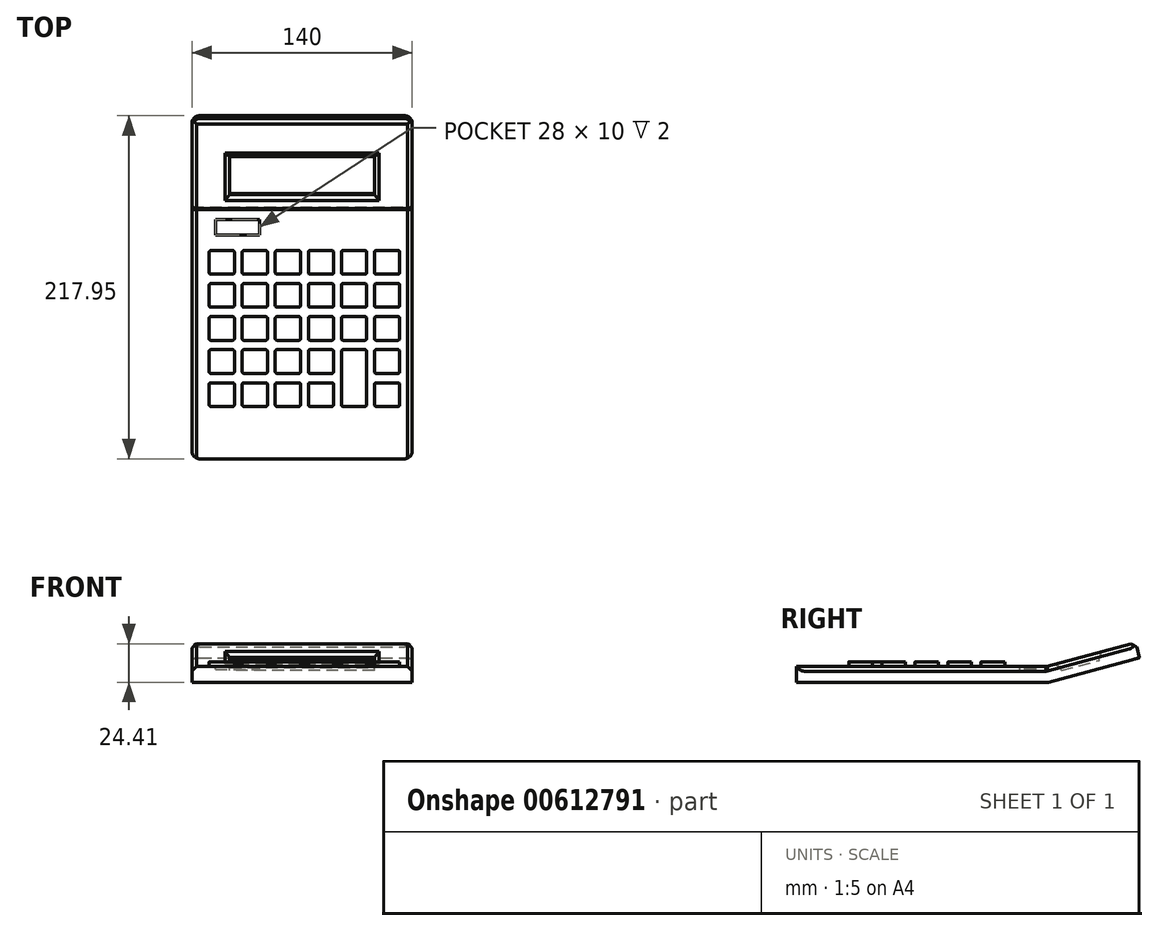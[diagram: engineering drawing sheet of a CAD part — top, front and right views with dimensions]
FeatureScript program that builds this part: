
annotation { "Feature Type Name" : "Feature", "Feature Type Description" : "" }
export const myFeature = defineFeature(function(context is Context, id is Id, definition is map)
    precondition{}
    {
        {
            var Q0;
            Q0=qCreatedBy(makeId("Right.planeOp"),FACE);
            var sketch = newSketch(context, id + "F0", { "sketchPlane" : qUnion([Q0])});
            skLineSegment(sketch, "E0", {"start": v(-151.78, 0) * mm, "end": v(8.22, 0) * mm});
            skLineSegment(sketch, "E1", {"start": v(8.22, 0) * mm, "end": v(66.17, 15.53) * mm});
            skLineSegment(sketch, "E2.0", {"start": v(6.9, 10) * mm, "end": v(63.58, 25.19) * mm});
            skLineSegment(sketch, "E2.1", {"start": v(-151.78, 10) * mm, "end": v(6.9, 10) * mm});
            skLineSegment(sketch, "E3", {"start": v(-151.78, 0) * mm, "end": v(-151.78, 10) * mm});
            skLineSegment(sketch, "E4", {"start": v(66.17, 15.53) * mm, "end": v(63.58, 25.19) * mm});
            skSolve(sketch);
        }
        {
            var Q0;
            Q0 = qSketchRegion(id + "F0", true);
            extrude(context, id + "F1", {"entities" : qUnion([Q0]), "endBound" : BoundingType.SYMMETRIC, "oppositeDirection" : true, "depth" : 140 * mm, "offsetDistance" : 25 * mm});
        }
        {
            var Q0;
            Q0=makeQuery(id+"F1.opExtrude","SWEPT_FACE",FACE,{"disambiguationData":[OSD([sQuery(id+"F0.wireOp",EDGE,"E2.0")])]});
            var sketch = newSketch(context, id + "F2", { "sketchPlane" : qUnion([Q0])});
            skLineSegment(sketch, "E5.bottom", {"start": v(46, 17.94) * mm, "end": v(-46, 17.94) * mm});
            skLineSegment(sketch, "E5.top", {"start": v(46, 42.94) * mm, "end": v(-46, 42.94) * mm});
            skLineSegment(sketch, "E5.left", {"start": v(46, 17.94) * mm, "end": v(46, 42.94) * mm});
            skLineSegment(sketch, "E5.right", {"start": v(-46, 17.94) * mm, "end": v(-46, 42.94) * mm});
            skPoint(sketch, "E5.middle", {"position": v(0, 30.44) * mm});
            skPoint(sketch, "E5.middle.positionSnap0", {"position": v(0, 9.25) * mm});
            skPoint(sketch, "E5.centerSnap0", {"position": v(0, 9.25) * mm});
            skSolve(sketch);
        }
        {
            var Q0;
            Q0 = qSketchRegion(id + "F2", true);
            extrude(context, id + "F3", {"entities" : qUnion([Q0]), "operationType" : NewBodyOperationType.REMOVE, "oppositeDirection" : true, "depth" : 5 * mm, "offsetDistance" : 25 * mm});
        }
        {
            var Q0;
            Q0=makeQuery(id+"F3.boolean.opBoolean","COPY",EDGE,{"derivedFrom":makeQuery(id+"F3.opExtrude","CAP_EDGE",EDGE,{"disambiguationData":[OSD([sQuery(id+"F2.wireOp",EDGE,"E5.right")])],"isStart":true})});
            var Q1;
            Q1=makeQuery(id+"F3.boolean.opBoolean","COPY",EDGE,{"derivedFrom":makeQuery(id+"F3.opExtrude","CAP_EDGE",EDGE,{"disambiguationData":[OSD([sQuery(id+"F2.wireOp",EDGE,"E5.top")])],"isStart":true})});
            var Q2;
            Q2=makeQuery(id+"F1.opExtrude","SWEPT_FACE",FACE,{"disambiguationData":[OSD([sQuery(id+"F0.wireOp",EDGE,"E2.0")])]});
            chamfer(context, id + "F4", {"entities" : qUnion([Q0, Q1, Q2]), "width" : 3 * mm, "tangentPropagation" : true});
        }
        {
            var Q0;
            Q0=makeQuery(id+"F1.opExtrude","CAP_EDGE",EDGE,{"disambiguationData":[OSD([sQuery(id+"F0.wireOp",EDGE,"E3")])],"isStart":false});
            var Q1;
            Q1=makeQuery(id+"F1.opExtrude","CAP_EDGE",EDGE,{"disambiguationData":[OSD([sQuery(id+"F0.wireOp",EDGE,"E3")])],"isStart":true});
            var Q2;
            Q2=makeQuery(id+"F1.opExtrude","CAP_EDGE",EDGE,{"disambiguationData":[OSD([sQuery(id+"F0.wireOp",EDGE,"E4")])],"isStart":false});
            var Q3;
            Q3=makeQuery(id+"F1.opExtrude","CAP_EDGE",EDGE,{"disambiguationData":[OSD([sQuery(id+"F0.wireOp",EDGE,"E4")])],"isStart":true});
            fillet(context, id + "F5", {"entities" : qUnion([Q0, Q1, Q2, Q3]), "radius" : 5 * mm, "tangentPropagation" : true, "allowEdgeOverflow" : false});
        }
        {
            var Q0;
            Q0=makeQuery(id+"F1.opExtrude","SWEPT_FACE",FACE,{"disambiguationData":[OSD([sQuery(id+"F0.wireOp",EDGE,"E2.1")])]});
            var sketch = newSketch(context, id + "F6", { "sketchPlane" : qUnion([Q0])});
            skLineSegment(sketch, "E6.bottom", {"start": v(-58, -19.5) * mm, "end": v(-44, -19.5) * mm});
            skLineSegment(sketch, "E6.top", {"start": v(-58, -34.5) * mm, "end": v(-44, -34.5) * mm});
            skLineSegment(sketch, "E6.left", {"start": v(-59, -20.5) * mm, "end": v(-59, -33.5) * mm});
            skLineSegment(sketch, "E6.right", {"start": v(-43, -20.5) * mm, "end": v(-43, -33.5) * mm});
            skLineSegment(sketch, "E7.bottom", {"start": v(-55, 0.28) * mm, "end": v(-27, 0.28) * mm});
            skLineSegment(sketch, "E7.top", {"start": v(-55, -9.72) * mm, "end": v(-27, -9.72) * mm});
            skLineSegment(sketch, "E7.left", {"start": v(-55, 0.28) * mm, "end": v(-55, -9.72) * mm});
            skLineSegment(sketch, "E7.right", {"start": v(-27, 0.28) * mm, "end": v(-27, -9.72) * mm});
            skPoint(sketch, "E8.visualSharp", {"position": v(-43, -19.5) * mm});
            skArc(sketch, "E8.filletArc", {"start": v(-43, -20.5) * mm, "mid": v(-43.3, -19.79) * mm, "end": v(-44, -19.5) * mm});
            skPoint(sketch, "E9.visualSharp", {"position": v(-43, -34.5) * mm});
            skArc(sketch, "E9.filletArc", {"start": v(-44, -34.5) * mm, "mid": v(-43.3, -34.2) * mm, "end": v(-43, -33.5) * mm});
            skPoint(sketch, "E10.visualSharp", {"position": v(-59, -34.5) * mm});
            skArc(sketch, "E10.filletArc", {"start": v(-59, -33.5) * mm, "mid": v(-58.7, -34.2) * mm, "end": v(-58, -34.5) * mm});
            skPoint(sketch, "E11.visualSharp", {"position": v(-59, -19.5) * mm});
            skArc(sketch, "E11.filletArc", {"start": v(-58, -19.5) * mm, "mid": v(-58.7, -19.79) * mm, "end": v(-59, -20.5) * mm});
            skPoint(sketch, "E12.1.0.0", {"position": v(-22, -19.5) * mm});
            skLineSegment(sketch, "E12.1.0.1", {"start": v(-38, -20.5) * mm, "end": v(-38, -33.5) * mm});
            skPoint(sketch, "E12.1.0.2", {"position": v(-22, -34.5) * mm});
            skLineSegment(sketch, "E12.1.0.3", {"start": v(-37, -34.5) * mm, "end": v(-23, -34.5) * mm});
            skLineSegment(sketch, "E12.1.0.4", {"start": v(-22, -20.5) * mm, "end": v(-22, -33.5) * mm});
            skLineSegment(sketch, "E12.1.0.5", {"start": v(-37, -19.5) * mm, "end": v(-23, -19.5) * mm});
            skPoint(sketch, "E12.1.0.6", {"position": v(-38, -19.5) * mm});
            skPoint(sketch, "E12.1.0.7", {"position": v(-38, -34.5) * mm});
            skArc(sketch, "E12.1.0.8", {"start": v(-23, -34.5) * mm, "mid": v(-22.3, -34.2) * mm, "end": v(-22, -33.5) * mm});
            skArc(sketch, "E12.1.0.9", {"start": v(-37, -19.5) * mm, "mid": v(-37.7, -19.79) * mm, "end": v(-38, -20.5) * mm});
            skArc(sketch, "E12.1.0.10", {"start": v(-38, -33.5) * mm, "mid": v(-37.7, -34.2) * mm, "end": v(-37, -34.5) * mm});
            skArc(sketch, "E12.1.0.11", {"start": v(-22, -20.5) * mm, "mid": v(-22.3, -19.79) * mm, "end": v(-23, -19.5) * mm});
            skPoint(sketch, "E12.2.0.0", {"position": v(-1, -19.5) * mm});
            skLineSegment(sketch, "E12.2.0.1", {"start": v(-17, -20.5) * mm, "end": v(-17, -33.5) * mm});
            skPoint(sketch, "E12.2.0.2", {"position": v(-1, -34.5) * mm});
            skLineSegment(sketch, "E12.2.0.3", {"start": v(-16, -34.5) * mm, "end": v(-2, -34.5) * mm});
            skLineSegment(sketch, "E12.2.0.4", {"start": v(-1, -20.5) * mm, "end": v(-1, -33.5) * mm});
            skLineSegment(sketch, "E12.2.0.5", {"start": v(-16, -19.5) * mm, "end": v(-2, -19.5) * mm});
            skPoint(sketch, "E12.2.0.6", {"position": v(-17, -19.5) * mm});
            skPoint(sketch, "E12.2.0.7", {"position": v(-17, -34.5) * mm});
            skArc(sketch, "E12.2.0.8", {"start": v(-2, -34.5) * mm, "mid": v(-1.3, -34.2) * mm, "end": v(-1, -33.5) * mm});
            skArc(sketch, "E12.2.0.9", {"start": v(-16, -19.5) * mm, "mid": v(-16.7, -19.79) * mm, "end": v(-17, -20.5) * mm});
            skArc(sketch, "E12.2.0.10", {"start": v(-17, -33.5) * mm, "mid": v(-16.7, -34.2) * mm, "end": v(-16, -34.5) * mm});
            skArc(sketch, "E12.2.0.11", {"start": v(-1, -20.5) * mm, "mid": v(-1.3, -19.79) * mm, "end": v(-2, -19.5) * mm});
            skPoint(sketch, "E12.3.0.0", {"position": v(20, -19.5) * mm});
            skLineSegment(sketch, "E12.3.0.1", {"start": v(4, -20.5) * mm, "end": v(4, -33.5) * mm});
            skPoint(sketch, "E12.3.0.2", {"position": v(20, -34.5) * mm});
            skLineSegment(sketch, "E12.3.0.3", {"start": v(5, -34.5) * mm, "end": v(19, -34.5) * mm});
            skLineSegment(sketch, "E12.3.0.4", {"start": v(20, -20.5) * mm, "end": v(20, -33.5) * mm});
            skLineSegment(sketch, "E12.3.0.5", {"start": v(5, -19.5) * mm, "end": v(19, -19.5) * mm});
            skPoint(sketch, "E12.3.0.6", {"position": v(4, -19.5) * mm});
            skPoint(sketch, "E12.3.0.7", {"position": v(4, -34.5) * mm});
            skArc(sketch, "E12.3.0.8", {"start": v(19, -34.5) * mm, "mid": v(19.7, -34.2) * mm, "end": v(20, -33.5) * mm});
            skArc(sketch, "E12.3.0.9", {"start": v(5, -19.5) * mm, "mid": v(4.3, -19.79) * mm, "end": v(4, -20.5) * mm});
            skArc(sketch, "E12.3.0.10", {"start": v(4, -33.5) * mm, "mid": v(4.3, -34.2) * mm, "end": v(5, -34.5) * mm});
            skArc(sketch, "E12.3.0.11", {"start": v(20, -20.5) * mm, "mid": v(19.7, -19.79) * mm, "end": v(19, -19.5) * mm});
            skPoint(sketch, "E12.4.0.0", {"position": v(41, -19.5) * mm});
            skLineSegment(sketch, "E12.4.0.1", {"start": v(25, -20.5) * mm, "end": v(25, -33.5) * mm});
            skPoint(sketch, "E12.4.0.2", {"position": v(41, -34.5) * mm});
            skLineSegment(sketch, "E12.4.0.3", {"start": v(26, -34.5) * mm, "end": v(40, -34.5) * mm});
            skLineSegment(sketch, "E12.4.0.4", {"start": v(41, -20.5) * mm, "end": v(41, -33.5) * mm});
            skLineSegment(sketch, "E12.4.0.5", {"start": v(26, -19.5) * mm, "end": v(40, -19.5) * mm});
            skPoint(sketch, "E12.4.0.6", {"position": v(25, -19.5) * mm});
            skPoint(sketch, "E12.4.0.7", {"position": v(25, -34.5) * mm});
            skArc(sketch, "E12.4.0.8", {"start": v(40, -34.5) * mm, "mid": v(40.7, -34.2) * mm, "end": v(41, -33.5) * mm});
            skArc(sketch, "E12.4.0.9", {"start": v(26, -19.5) * mm, "mid": v(25.3, -19.79) * mm, "end": v(25, -20.5) * mm});
            skArc(sketch, "E12.4.0.10", {"start": v(25, -33.5) * mm, "mid": v(25.3, -34.2) * mm, "end": v(26, -34.5) * mm});
            skArc(sketch, "E12.4.0.11", {"start": v(41, -20.5) * mm, "mid": v(40.7, -19.79) * mm, "end": v(40, -19.5) * mm});
            skPoint(sketch, "E12.5.0.0", {"position": v(62, -19.5) * mm});
            skLineSegment(sketch, "E12.5.0.1", {"start": v(46, -20.5) * mm, "end": v(46, -33.5) * mm});
            skPoint(sketch, "E12.5.0.2", {"position": v(62, -34.5) * mm});
            skLineSegment(sketch, "E12.5.0.3", {"start": v(47, -34.5) * mm, "end": v(61, -34.5) * mm});
            skLineSegment(sketch, "E12.5.0.4", {"start": v(62, -20.5) * mm, "end": v(62, -33.5) * mm});
            skLineSegment(sketch, "E12.5.0.5", {"start": v(47, -19.5) * mm, "end": v(61, -19.5) * mm});
            skPoint(sketch, "E12.5.0.6", {"position": v(46, -19.5) * mm});
            skPoint(sketch, "E12.5.0.7", {"position": v(46, -34.5) * mm});
            skArc(sketch, "E12.5.0.8", {"start": v(61, -34.5) * mm, "mid": v(61.7, -34.2) * mm, "end": v(62, -33.5) * mm});
            skArc(sketch, "E12.5.0.9", {"start": v(47, -19.5) * mm, "mid": v(46.3, -19.79) * mm, "end": v(46, -20.5) * mm});
            skArc(sketch, "E12.5.0.10", {"start": v(46, -33.5) * mm, "mid": v(46.3, -34.2) * mm, "end": v(47, -34.5) * mm});
            skArc(sketch, "E12.5.0.11", {"start": v(62, -20.5) * mm, "mid": v(61.7, -19.79) * mm, "end": v(61, -19.5) * mm});
            skLineSegment(sketch, "E12.direction1", {"start": v(-59, -34.5) * mm, "end": v(-38, -34.5) * mm, "construction": true});
            skPoint(sketch, "E13.0.1.0", {"position": v(-59, -40.5) * mm});
            skLineSegment(sketch, "E13.0.1.1", {"start": v(26, -40.5) * mm, "end": v(40, -40.5) * mm});
            skLineSegment(sketch, "E13.0.1.2", {"start": v(-16, -40.5) * mm, "end": v(-2, -40.5) * mm});
            skPoint(sketch, "E13.0.1.3", {"position": v(4, -40.5) * mm});
            skLineSegment(sketch, "E13.0.1.4", {"start": v(5, -55.5) * mm, "end": v(19, -55.5) * mm});
            skPoint(sketch, "E13.0.1.5", {"position": v(62, -40.5) * mm});
            skPoint(sketch, "E13.0.1.6", {"position": v(-1, -40.5) * mm});
            skLineSegment(sketch, "E13.0.1.7", {"start": v(-59, -55.5) * mm, "end": v(-38, -55.5) * mm, "construction": true});
            skPoint(sketch, "E13.0.1.8", {"position": v(-22, -40.5) * mm});
            skPoint(sketch, "E13.0.1.9", {"position": v(-22, -55.5) * mm});
            skPoint(sketch, "E13.0.1.10", {"position": v(25, -55.5) * mm});
            skPoint(sketch, "E13.0.1.11", {"position": v(20, -55.5) * mm});
            skPoint(sketch, "E13.0.1.12", {"position": v(-17, -55.5) * mm});
            skPoint(sketch, "E13.0.1.13", {"position": v(20, -40.5) * mm});
            skLineSegment(sketch, "E13.0.1.14", {"start": v(25, -41.5) * mm, "end": v(25, -54.5) * mm});
            skPoint(sketch, "E13.0.1.15", {"position": v(62, -55.5) * mm});
            skPoint(sketch, "E13.0.1.16", {"position": v(41, -40.5) * mm});
            skLineSegment(sketch, "E13.0.1.17", {"start": v(-17, -41.5) * mm, "end": v(-17, -54.5) * mm});
            skLineSegment(sketch, "E13.0.1.18", {"start": v(47, -55.5) * mm, "end": v(61, -55.5) * mm});
            skPoint(sketch, "E13.0.1.19", {"position": v(46, -40.5) * mm});
            skPoint(sketch, "E13.0.1.20", {"position": v(-38, -40.5) * mm});
            skPoint(sketch, "E13.0.1.21", {"position": v(41, -55.5) * mm});
            skPoint(sketch, "E13.0.1.22", {"position": v(-1, -55.5) * mm});
            skPoint(sketch, "E13.0.1.23", {"position": v(-38, -55.5) * mm});
            skPoint(sketch, "E13.0.1.24", {"position": v(-59, -55.5) * mm});
            skPoint(sketch, "E13.0.1.25", {"position": v(46, -55.5) * mm});
            skPoint(sketch, "E13.0.1.26", {"position": v(4, -55.5) * mm});
            skLineSegment(sketch, "E13.0.1.27", {"start": v(46, -41.5) * mm, "end": v(46, -54.5) * mm});
            skLineSegment(sketch, "E13.0.1.28", {"start": v(4, -41.5) * mm, "end": v(4, -54.5) * mm});
            skLineSegment(sketch, "E13.0.1.29", {"start": v(62, -41.5) * mm, "end": v(62, -54.5) * mm});
            skLineSegment(sketch, "E13.0.1.30", {"start": v(26, -55.5) * mm, "end": v(40, -55.5) * mm});
            skLineSegment(sketch, "E13.0.1.31", {"start": v(20, -41.5) * mm, "end": v(20, -54.5) * mm});
            skLineSegment(sketch, "E13.0.1.32", {"start": v(-16, -55.5) * mm, "end": v(-2, -55.5) * mm});
            skPoint(sketch, "E13.0.1.33", {"position": v(25, -40.5) * mm});
            skPoint(sketch, "E13.0.1.34", {"position": v(-17, -40.5) * mm});
            skPoint(sketch, "E13.0.1.35", {"position": v(-43, -55.5) * mm});
            skLineSegment(sketch, "E13.0.1.36", {"start": v(-37, -55.5) * mm, "end": v(-23, -55.5) * mm});
            skLineSegment(sketch, "E13.0.1.37", {"start": v(-22, -41.5) * mm, "end": v(-22, -54.5) * mm});
            skLineSegment(sketch, "E13.0.1.38", {"start": v(-37, -40.5) * mm, "end": v(-23, -40.5) * mm});
            skLineSegment(sketch, "E13.0.1.39", {"start": v(-59, -41.5) * mm, "end": v(-59, -54.5) * mm});
            skLineSegment(sketch, "E13.0.1.40", {"start": v(-43, -41.5) * mm, "end": v(-43, -54.5) * mm});
            skLineSegment(sketch, "E13.0.1.41", {"start": v(47, -40.5) * mm, "end": v(61, -40.5) * mm});
            skLineSegment(sketch, "E13.0.1.42", {"start": v(41, -41.5) * mm, "end": v(41, -54.5) * mm});
            skLineSegment(sketch, "E13.0.1.43", {"start": v(5, -40.5) * mm, "end": v(19, -40.5) * mm});
            skLineSegment(sketch, "E13.0.1.44", {"start": v(-1, -41.5) * mm, "end": v(-1, -54.5) * mm});
            skLineSegment(sketch, "E13.0.1.45", {"start": v(-38, -41.5) * mm, "end": v(-38, -54.5) * mm});
            skPoint(sketch, "E13.0.1.46", {"position": v(-43, -40.5) * mm});
            skLineSegment(sketch, "E13.0.1.47", {"start": v(-58, -40.5) * mm, "end": v(-44, -40.5) * mm});
            skLineSegment(sketch, "E13.0.1.48", {"start": v(-58, -55.5) * mm, "end": v(-44, -55.5) * mm});
            skArc(sketch, "E13.0.1.49", {"start": v(19, -55.5) * mm, "mid": v(19.7, -55.2) * mm, "end": v(20, -54.5) * mm});
            skArc(sketch, "E13.0.1.50", {"start": v(62, -41.5) * mm, "mid": v(61.7, -40.79) * mm, "end": v(61, -40.5) * mm});
            skArc(sketch, "E13.0.1.51", {"start": v(47, -40.5) * mm, "mid": v(46.3, -40.79) * mm, "end": v(46, -41.5) * mm});
            skArc(sketch, "E13.0.1.52", {"start": v(25, -54.5) * mm, "mid": v(25.3, -55.2) * mm, "end": v(26, -55.5) * mm});
            skArc(sketch, "E13.0.1.53", {"start": v(20, -41.5) * mm, "mid": v(19.7, -40.79) * mm, "end": v(19, -40.5) * mm});
            skArc(sketch, "E13.0.1.54", {"start": v(-37, -40.5) * mm, "mid": v(-37.7, -40.79) * mm, "end": v(-38, -41.5) * mm});
            skArc(sketch, "E13.0.1.55", {"start": v(-2, -55.5) * mm, "mid": v(-1.3, -55.2) * mm, "end": v(-1, -54.5) * mm});
            skArc(sketch, "E13.0.1.56", {"start": v(5, -40.5) * mm, "mid": v(4.3, -40.79) * mm, "end": v(4, -41.5) * mm});
            skArc(sketch, "E13.0.1.57", {"start": v(61, -55.5) * mm, "mid": v(61.7, -55.2) * mm, "end": v(62, -54.5) * mm});
            skArc(sketch, "E13.0.1.58", {"start": v(-17, -54.5) * mm, "mid": v(-16.7, -55.2) * mm, "end": v(-16, -55.5) * mm});
            skArc(sketch, "E13.0.1.59", {"start": v(4, -54.5) * mm, "mid": v(4.3, -55.2) * mm, "end": v(5, -55.5) * mm});
            skArc(sketch, "E13.0.1.60", {"start": v(40, -55.5) * mm, "mid": v(40.7, -55.2) * mm, "end": v(41, -54.5) * mm});
            skArc(sketch, "E13.0.1.61", {"start": v(-23, -55.5) * mm, "mid": v(-22.3, -55.2) * mm, "end": v(-22, -54.5) * mm});
            skArc(sketch, "E13.0.1.62", {"start": v(-38, -54.5) * mm, "mid": v(-37.7, -55.2) * mm, "end": v(-37, -55.5) * mm});
            skArc(sketch, "E13.0.1.63", {"start": v(-22, -41.5) * mm, "mid": v(-22.3, -40.79) * mm, "end": v(-23, -40.5) * mm});
            skArc(sketch, "E13.0.1.64", {"start": v(46, -54.5) * mm, "mid": v(46.3, -55.2) * mm, "end": v(47, -55.5) * mm});
            skArc(sketch, "E13.0.1.65", {"start": v(41, -41.5) * mm, "mid": v(40.7, -40.79) * mm, "end": v(40, -40.5) * mm});
            skArc(sketch, "E13.0.1.66", {"start": v(-1, -41.5) * mm, "mid": v(-1.3, -40.79) * mm, "end": v(-2, -40.5) * mm});
            skArc(sketch, "E13.0.1.67", {"start": v(-44, -55.5) * mm, "mid": v(-43.3, -55.2) * mm, "end": v(-43, -54.5) * mm});
            skArc(sketch, "E13.0.1.68", {"start": v(-58, -40.5) * mm, "mid": v(-58.7, -40.79) * mm, "end": v(-59, -41.5) * mm});
            skArc(sketch, "E13.0.1.69", {"start": v(26, -40.5) * mm, "mid": v(25.3, -40.79) * mm, "end": v(25, -41.5) * mm});
            skArc(sketch, "E13.0.1.70", {"start": v(-16, -40.5) * mm, "mid": v(-16.7, -40.79) * mm, "end": v(-17, -41.5) * mm});
            skArc(sketch, "E13.0.1.71", {"start": v(-43, -41.5) * mm, "mid": v(-43.3, -40.79) * mm, "end": v(-44, -40.5) * mm});
            skArc(sketch, "E13.0.1.72", {"start": v(-59, -54.5) * mm, "mid": v(-58.7, -55.2) * mm, "end": v(-58, -55.5) * mm});
            skPoint(sketch, "E13.0.2.0", {"position": v(-59, -61.5) * mm});
            skLineSegment(sketch, "E13.0.2.1", {"start": v(26, -61.5) * mm, "end": v(40, -61.5) * mm});
            skLineSegment(sketch, "E13.0.2.2", {"start": v(-16, -61.5) * mm, "end": v(-2, -61.5) * mm});
            skPoint(sketch, "E13.0.2.3", {"position": v(4, -61.5) * mm});
            skLineSegment(sketch, "E13.0.2.4", {"start": v(5, -76.5) * mm, "end": v(19, -76.5) * mm});
            skPoint(sketch, "E13.0.2.5", {"position": v(62, -61.5) * mm});
            skPoint(sketch, "E13.0.2.6", {"position": v(-1, -61.5) * mm});
            skLineSegment(sketch, "E13.0.2.7", {"start": v(-59, -76.5) * mm, "end": v(-38, -76.5) * mm, "construction": true});
            skPoint(sketch, "E13.0.2.8", {"position": v(-22, -61.5) * mm});
            skPoint(sketch, "E13.0.2.9", {"position": v(-22, -76.5) * mm});
            skPoint(sketch, "E13.0.2.10", {"position": v(25, -76.5) * mm});
            skPoint(sketch, "E13.0.2.11", {"position": v(20, -76.5) * mm});
            skPoint(sketch, "E13.0.2.12", {"position": v(-17, -76.5) * mm});
            skPoint(sketch, "E13.0.2.13", {"position": v(20, -61.5) * mm});
            skLineSegment(sketch, "E13.0.2.14", {"start": v(25, -62.5) * mm, "end": v(25, -75.5) * mm});
            skPoint(sketch, "E13.0.2.15", {"position": v(62, -76.5) * mm});
            skPoint(sketch, "E13.0.2.16", {"position": v(41, -61.5) * mm});
            skLineSegment(sketch, "E13.0.2.17", {"start": v(-17, -62.5) * mm, "end": v(-17, -75.5) * mm});
            skLineSegment(sketch, "E13.0.2.18", {"start": v(47, -76.5) * mm, "end": v(61, -76.5) * mm});
            skPoint(sketch, "E13.0.2.19", {"position": v(46, -61.5) * mm});
            skPoint(sketch, "E13.0.2.20", {"position": v(-38, -61.5) * mm});
            skPoint(sketch, "E13.0.2.21", {"position": v(41, -76.5) * mm});
            skPoint(sketch, "E13.0.2.22", {"position": v(-1, -76.5) * mm});
            skPoint(sketch, "E13.0.2.23", {"position": v(-38, -76.5) * mm});
            skPoint(sketch, "E13.0.2.24", {"position": v(-59, -76.5) * mm});
            skPoint(sketch, "E13.0.2.25", {"position": v(46, -76.5) * mm});
            skPoint(sketch, "E13.0.2.26", {"position": v(4, -76.5) * mm});
            skLineSegment(sketch, "E13.0.2.27", {"start": v(46, -62.5) * mm, "end": v(46, -75.5) * mm});
            skLineSegment(sketch, "E13.0.2.28", {"start": v(4, -62.5) * mm, "end": v(4, -75.5) * mm});
            skLineSegment(sketch, "E13.0.2.29", {"start": v(62, -62.5) * mm, "end": v(62, -75.5) * mm});
            skLineSegment(sketch, "E13.0.2.30", {"start": v(26, -76.5) * mm, "end": v(40, -76.5) * mm});
            skLineSegment(sketch, "E13.0.2.31", {"start": v(20, -62.5) * mm, "end": v(20, -75.5) * mm});
            skLineSegment(sketch, "E13.0.2.32", {"start": v(-16, -76.5) * mm, "end": v(-2, -76.5) * mm});
            skPoint(sketch, "E13.0.2.33", {"position": v(25, -61.5) * mm});
            skPoint(sketch, "E13.0.2.34", {"position": v(-17, -61.5) * mm});
            skPoint(sketch, "E13.0.2.35", {"position": v(-43, -76.5) * mm});
            skLineSegment(sketch, "E13.0.2.36", {"start": v(-37, -76.5) * mm, "end": v(-23, -76.5) * mm});
            skLineSegment(sketch, "E13.0.2.37", {"start": v(-22, -62.5) * mm, "end": v(-22, -75.5) * mm});
            skLineSegment(sketch, "E13.0.2.38", {"start": v(-37, -61.5) * mm, "end": v(-23, -61.5) * mm});
            skLineSegment(sketch, "E13.0.2.39", {"start": v(-59, -62.5) * mm, "end": v(-59, -75.5) * mm});
            skLineSegment(sketch, "E13.0.2.40", {"start": v(-43, -62.5) * mm, "end": v(-43, -75.5) * mm});
            skLineSegment(sketch, "E13.0.2.41", {"start": v(47, -61.5) * mm, "end": v(61, -61.5) * mm});
            skLineSegment(sketch, "E13.0.2.42", {"start": v(41, -62.5) * mm, "end": v(41, -75.5) * mm});
            skLineSegment(sketch, "E13.0.2.43", {"start": v(5, -61.5) * mm, "end": v(19, -61.5) * mm});
            skLineSegment(sketch, "E13.0.2.44", {"start": v(-1, -62.5) * mm, "end": v(-1, -75.5) * mm});
            skLineSegment(sketch, "E13.0.2.45", {"start": v(-38, -62.5) * mm, "end": v(-38, -75.5) * mm});
            skPoint(sketch, "E13.0.2.46", {"position": v(-43, -61.5) * mm});
            skLineSegment(sketch, "E13.0.2.47", {"start": v(-58, -61.5) * mm, "end": v(-44, -61.5) * mm});
            skLineSegment(sketch, "E13.0.2.48", {"start": v(-58, -76.5) * mm, "end": v(-44, -76.5) * mm});
            skArc(sketch, "E13.0.2.49", {"start": v(19, -76.5) * mm, "mid": v(19.7, -76.2) * mm, "end": v(20, -75.5) * mm});
            skArc(sketch, "E13.0.2.50", {"start": v(62, -62.5) * mm, "mid": v(61.7, -61.79) * mm, "end": v(61, -61.5) * mm});
            skArc(sketch, "E13.0.2.51", {"start": v(47, -61.5) * mm, "mid": v(46.3, -61.79) * mm, "end": v(46, -62.5) * mm});
            skArc(sketch, "E13.0.2.52", {"start": v(25, -75.5) * mm, "mid": v(25.3, -76.2) * mm, "end": v(26, -76.5) * mm});
            skArc(sketch, "E13.0.2.53", {"start": v(20, -62.5) * mm, "mid": v(19.7, -61.79) * mm, "end": v(19, -61.5) * mm});
            skArc(sketch, "E13.0.2.54", {"start": v(-37, -61.5) * mm, "mid": v(-37.7, -61.79) * mm, "end": v(-38, -62.5) * mm});
            skArc(sketch, "E13.0.2.55", {"start": v(-2, -76.5) * mm, "mid": v(-1.3, -76.2) * mm, "end": v(-1, -75.5) * mm});
            skArc(sketch, "E13.0.2.56", {"start": v(5, -61.5) * mm, "mid": v(4.3, -61.79) * mm, "end": v(4, -62.5) * mm});
            skArc(sketch, "E13.0.2.57", {"start": v(61, -76.5) * mm, "mid": v(61.7, -76.2) * mm, "end": v(62, -75.5) * mm});
            skArc(sketch, "E13.0.2.58", {"start": v(-17, -75.5) * mm, "mid": v(-16.7, -76.2) * mm, "end": v(-16, -76.5) * mm});
            skArc(sketch, "E13.0.2.59", {"start": v(4, -75.5) * mm, "mid": v(4.3, -76.2) * mm, "end": v(5, -76.5) * mm});
            skArc(sketch, "E13.0.2.60", {"start": v(40, -76.5) * mm, "mid": v(40.7, -76.2) * mm, "end": v(41, -75.5) * mm});
            skArc(sketch, "E13.0.2.61", {"start": v(-23, -76.5) * mm, "mid": v(-22.3, -76.2) * mm, "end": v(-22, -75.5) * mm});
            skArc(sketch, "E13.0.2.62", {"start": v(-38, -75.5) * mm, "mid": v(-37.7, -76.2) * mm, "end": v(-37, -76.5) * mm});
            skArc(sketch, "E13.0.2.63", {"start": v(-22, -62.5) * mm, "mid": v(-22.3, -61.79) * mm, "end": v(-23, -61.5) * mm});
            skArc(sketch, "E13.0.2.64", {"start": v(46, -75.5) * mm, "mid": v(46.3, -76.2) * mm, "end": v(47, -76.5) * mm});
            skArc(sketch, "E13.0.2.65", {"start": v(41, -62.5) * mm, "mid": v(40.7, -61.79) * mm, "end": v(40, -61.5) * mm});
            skArc(sketch, "E13.0.2.66", {"start": v(-1, -62.5) * mm, "mid": v(-1.3, -61.79) * mm, "end": v(-2, -61.5) * mm});
            skArc(sketch, "E13.0.2.67", {"start": v(-44, -76.5) * mm, "mid": v(-43.3, -76.2) * mm, "end": v(-43, -75.5) * mm});
            skArc(sketch, "E13.0.2.68", {"start": v(-58, -61.5) * mm, "mid": v(-58.7, -61.79) * mm, "end": v(-59, -62.5) * mm});
            skArc(sketch, "E13.0.2.69", {"start": v(26, -61.5) * mm, "mid": v(25.3, -61.79) * mm, "end": v(25, -62.5) * mm});
            skArc(sketch, "E13.0.2.70", {"start": v(-16, -61.5) * mm, "mid": v(-16.7, -61.79) * mm, "end": v(-17, -62.5) * mm});
            skArc(sketch, "E13.0.2.71", {"start": v(-43, -62.5) * mm, "mid": v(-43.3, -61.79) * mm, "end": v(-44, -61.5) * mm});
            skArc(sketch, "E13.0.2.72", {"start": v(-59, -75.5) * mm, "mid": v(-58.7, -76.2) * mm, "end": v(-58, -76.5) * mm});
            skPoint(sketch, "E13.0.3.0", {"position": v(-59, -82.5) * mm});
            skLineSegment(sketch, "E13.0.3.1", {"start": v(26, -82.5) * mm, "end": v(40, -82.5) * mm});
            skLineSegment(sketch, "E13.0.3.2", {"start": v(-16, -82.5) * mm, "end": v(-2, -82.5) * mm});
            skPoint(sketch, "E13.0.3.3", {"position": v(4, -82.5) * mm});
            skLineSegment(sketch, "E13.0.3.4", {"start": v(5, -97.5) * mm, "end": v(19, -97.5) * mm});
            skPoint(sketch, "E13.0.3.5", {"position": v(62, -82.5) * mm});
            skPoint(sketch, "E13.0.3.6", {"position": v(-1, -82.5) * mm});
            skLineSegment(sketch, "E13.0.3.7", {"start": v(-59, -97.5) * mm, "end": v(-38, -97.5) * mm, "construction": true});
            skPoint(sketch, "E13.0.3.8", {"position": v(-22, -82.5) * mm});
            skPoint(sketch, "E13.0.3.9", {"position": v(-22, -97.5) * mm});
            skPoint(sketch, "E13.0.3.10", {"position": v(25, -97.5) * mm});
            skPoint(sketch, "E13.0.3.11", {"position": v(20, -97.5) * mm});
            skPoint(sketch, "E13.0.3.12", {"position": v(-17, -97.5) * mm});
            skPoint(sketch, "E13.0.3.13", {"position": v(20, -82.5) * mm});
            skLineSegment(sketch, "E13.0.3.14", {"start": v(25, -83.5) * mm, "end": v(25, -96.5) * mm});
            skPoint(sketch, "E13.0.3.15", {"position": v(62, -97.5) * mm});
            skPoint(sketch, "E13.0.3.16", {"position": v(41, -82.5) * mm});
            skLineSegment(sketch, "E13.0.3.17", {"start": v(-17, -83.5) * mm, "end": v(-17, -96.5) * mm});
            skLineSegment(sketch, "E13.0.3.18", {"start": v(47, -97.5) * mm, "end": v(61, -97.5) * mm});
            skPoint(sketch, "E13.0.3.19", {"position": v(46, -82.5) * mm});
            skPoint(sketch, "E13.0.3.20", {"position": v(-38, -82.5) * mm});
            skPoint(sketch, "E13.0.3.21", {"position": v(41, -97.5) * mm});
            skPoint(sketch, "E13.0.3.22", {"position": v(-1, -97.5) * mm});
            skPoint(sketch, "E13.0.3.23", {"position": v(-38, -97.5) * mm});
            skPoint(sketch, "E13.0.3.24", {"position": v(-59, -97.5) * mm});
            skPoint(sketch, "E13.0.3.25", {"position": v(46, -97.5) * mm});
            skPoint(sketch, "E13.0.3.26", {"position": v(4, -97.5) * mm});
            skLineSegment(sketch, "E13.0.3.27", {"start": v(46, -83.5) * mm, "end": v(46, -96.5) * mm});
            skLineSegment(sketch, "E13.0.3.28", {"start": v(4, -83.5) * mm, "end": v(4, -96.5) * mm});
            skLineSegment(sketch, "E13.0.3.29", {"start": v(62, -83.5) * mm, "end": v(62, -96.5) * mm});
            skLineSegment(sketch, "E13.0.3.30", {"start": v(26, -97.5) * mm, "end": v(40, -97.5) * mm});
            skLineSegment(sketch, "E13.0.3.31", {"start": v(20, -83.5) * mm, "end": v(20, -96.5) * mm});
            skLineSegment(sketch, "E13.0.3.32", {"start": v(-16, -97.5) * mm, "end": v(-2, -97.5) * mm});
            skPoint(sketch, "E13.0.3.33", {"position": v(25, -82.5) * mm});
            skPoint(sketch, "E13.0.3.34", {"position": v(-17, -82.5) * mm});
            skPoint(sketch, "E13.0.3.35", {"position": v(-43, -97.5) * mm});
            skLineSegment(sketch, "E13.0.3.36", {"start": v(-37, -97.5) * mm, "end": v(-23, -97.5) * mm});
            skLineSegment(sketch, "E13.0.3.37", {"start": v(-22, -83.5) * mm, "end": v(-22, -96.5) * mm});
            skLineSegment(sketch, "E13.0.3.38", {"start": v(-37, -82.5) * mm, "end": v(-23, -82.5) * mm});
            skLineSegment(sketch, "E13.0.3.39", {"start": v(-59, -83.5) * mm, "end": v(-59, -96.5) * mm});
            skLineSegment(sketch, "E13.0.3.40", {"start": v(-43, -83.5) * mm, "end": v(-43, -96.5) * mm});
            skLineSegment(sketch, "E13.0.3.41", {"start": v(47, -82.5) * mm, "end": v(61, -82.5) * mm});
            skLineSegment(sketch, "E13.0.3.42", {"start": v(41, -83.5) * mm, "end": v(41, -96.5) * mm});
            skLineSegment(sketch, "E13.0.3.43", {"start": v(5, -82.5) * mm, "end": v(19, -82.5) * mm});
            skLineSegment(sketch, "E13.0.3.44", {"start": v(-1, -83.5) * mm, "end": v(-1, -96.5) * mm});
            skLineSegment(sketch, "E13.0.3.45", {"start": v(-38, -83.5) * mm, "end": v(-38, -96.5) * mm});
            skPoint(sketch, "E13.0.3.46", {"position": v(-43, -82.5) * mm});
            skLineSegment(sketch, "E13.0.3.47", {"start": v(-58, -82.5) * mm, "end": v(-44, -82.5) * mm});
            skLineSegment(sketch, "E13.0.3.48", {"start": v(-58, -97.5) * mm, "end": v(-44, -97.5) * mm});
            skArc(sketch, "E13.0.3.49", {"start": v(19, -97.5) * mm, "mid": v(19.7, -97.2) * mm, "end": v(20, -96.5) * mm});
            skArc(sketch, "E13.0.3.50", {"start": v(62, -83.5) * mm, "mid": v(61.7, -82.79) * mm, "end": v(61, -82.5) * mm});
            skArc(sketch, "E13.0.3.51", {"start": v(47, -82.5) * mm, "mid": v(46.3, -82.79) * mm, "end": v(46, -83.5) * mm});
            skArc(sketch, "E13.0.3.52", {"start": v(25, -96.5) * mm, "mid": v(25.3, -97.2) * mm, "end": v(26, -97.5) * mm});
            skArc(sketch, "E13.0.3.53", {"start": v(20, -83.5) * mm, "mid": v(19.7, -82.79) * mm, "end": v(19, -82.5) * mm});
            skArc(sketch, "E13.0.3.54", {"start": v(-37, -82.5) * mm, "mid": v(-37.7, -82.79) * mm, "end": v(-38, -83.5) * mm});
            skArc(sketch, "E13.0.3.55", {"start": v(-2, -97.5) * mm, "mid": v(-1.3, -97.2) * mm, "end": v(-1, -96.5) * mm});
            skArc(sketch, "E13.0.3.56", {"start": v(5, -82.5) * mm, "mid": v(4.3, -82.79) * mm, "end": v(4, -83.5) * mm});
            skArc(sketch, "E13.0.3.57", {"start": v(61, -97.5) * mm, "mid": v(61.7, -97.2) * mm, "end": v(62, -96.5) * mm});
            skArc(sketch, "E13.0.3.58", {"start": v(-17, -96.5) * mm, "mid": v(-16.7, -97.2) * mm, "end": v(-16, -97.5) * mm});
            skArc(sketch, "E13.0.3.59", {"start": v(4, -96.5) * mm, "mid": v(4.3, -97.2) * mm, "end": v(5, -97.5) * mm});
            skArc(sketch, "E13.0.3.60", {"start": v(40, -97.5) * mm, "mid": v(40.7, -97.2) * mm, "end": v(41, -96.5) * mm});
            skArc(sketch, "E13.0.3.61", {"start": v(-23, -97.5) * mm, "mid": v(-22.3, -97.2) * mm, "end": v(-22, -96.5) * mm});
            skArc(sketch, "E13.0.3.62", {"start": v(-38, -96.5) * mm, "mid": v(-37.7, -97.2) * mm, "end": v(-37, -97.5) * mm});
            skArc(sketch, "E13.0.3.63", {"start": v(-22, -83.5) * mm, "mid": v(-22.3, -82.79) * mm, "end": v(-23, -82.5) * mm});
            skArc(sketch, "E13.0.3.64", {"start": v(46, -96.5) * mm, "mid": v(46.3, -97.2) * mm, "end": v(47, -97.5) * mm});
            skArc(sketch, "E13.0.3.65", {"start": v(41, -83.5) * mm, "mid": v(40.7, -82.79) * mm, "end": v(40, -82.5) * mm});
            skArc(sketch, "E13.0.3.66", {"start": v(-1, -83.5) * mm, "mid": v(-1.3, -82.79) * mm, "end": v(-2, -82.5) * mm});
            skArc(sketch, "E13.0.3.67", {"start": v(-44, -97.5) * mm, "mid": v(-43.3, -97.2) * mm, "end": v(-43, -96.5) * mm});
            skArc(sketch, "E13.0.3.68", {"start": v(-58, -82.5) * mm, "mid": v(-58.7, -82.79) * mm, "end": v(-59, -83.5) * mm});
            skArc(sketch, "E13.0.3.69", {"start": v(26, -82.5) * mm, "mid": v(25.3, -82.79) * mm, "end": v(25, -83.5) * mm});
            skArc(sketch, "E13.0.3.70", {"start": v(-16, -82.5) * mm, "mid": v(-16.7, -82.79) * mm, "end": v(-17, -83.5) * mm});
            skArc(sketch, "E13.0.3.71", {"start": v(-43, -83.5) * mm, "mid": v(-43.3, -82.79) * mm, "end": v(-44, -82.5) * mm});
            skArc(sketch, "E13.0.3.72", {"start": v(-59, -96.5) * mm, "mid": v(-58.7, -97.2) * mm, "end": v(-58, -97.5) * mm});
            skPoint(sketch, "E13.0.4.0", {"position": v(-59, -103.5) * mm});
            skLineSegment(sketch, "E13.0.4.1", {"start": v(26, -103.5) * mm, "end": v(40, -103.5) * mm});
            skLineSegment(sketch, "E13.0.4.2", {"start": v(-16, -103.5) * mm, "end": v(-2, -103.5) * mm});
            skPoint(sketch, "E13.0.4.3", {"position": v(4, -103.5) * mm});
            skLineSegment(sketch, "E13.0.4.4", {"start": v(5, -118.5) * mm, "end": v(19, -118.5) * mm});
            skPoint(sketch, "E13.0.4.5", {"position": v(62, -103.5) * mm});
            skPoint(sketch, "E13.0.4.6", {"position": v(-1, -103.5) * mm});
            skLineSegment(sketch, "E13.0.4.7", {"start": v(-59, -118.5) * mm, "end": v(-38, -118.5) * mm, "construction": true});
            skPoint(sketch, "E13.0.4.8", {"position": v(-22, -103.5) * mm});
            skPoint(sketch, "E13.0.4.9", {"position": v(-22, -118.5) * mm});
            skPoint(sketch, "E13.0.4.10", {"position": v(25, -118.5) * mm});
            skPoint(sketch, "E13.0.4.11", {"position": v(20, -118.5) * mm});
            skPoint(sketch, "E13.0.4.12", {"position": v(-17, -118.5) * mm});
            skPoint(sketch, "E13.0.4.13", {"position": v(20, -103.5) * mm});
            skLineSegment(sketch, "E13.0.4.14", {"start": v(25, -104.5) * mm, "end": v(25, -117.5) * mm});
            skPoint(sketch, "E13.0.4.15", {"position": v(62, -118.5) * mm});
            skPoint(sketch, "E13.0.4.16", {"position": v(41, -103.5) * mm});
            skLineSegment(sketch, "E13.0.4.17", {"start": v(-17, -104.5) * mm, "end": v(-17, -117.5) * mm});
            skLineSegment(sketch, "E13.0.4.18", {"start": v(47, -118.5) * mm, "end": v(61, -118.5) * mm});
            skPoint(sketch, "E13.0.4.19", {"position": v(46, -103.5) * mm});
            skPoint(sketch, "E13.0.4.20", {"position": v(-38, -103.5) * mm});
            skPoint(sketch, "E13.0.4.21", {"position": v(41, -118.5) * mm});
            skPoint(sketch, "E13.0.4.22", {"position": v(-1, -118.5) * mm});
            skPoint(sketch, "E13.0.4.23", {"position": v(-38, -118.5) * mm});
            skPoint(sketch, "E13.0.4.24", {"position": v(-59, -118.5) * mm});
            skPoint(sketch, "E13.0.4.25", {"position": v(46, -118.5) * mm});
            skPoint(sketch, "E13.0.4.26", {"position": v(4, -118.5) * mm});
            skLineSegment(sketch, "E13.0.4.27", {"start": v(46, -104.5) * mm, "end": v(46, -117.5) * mm});
            skLineSegment(sketch, "E13.0.4.28", {"start": v(4, -104.5) * mm, "end": v(4, -117.5) * mm});
            skLineSegment(sketch, "E13.0.4.29", {"start": v(62, -104.5) * mm, "end": v(62, -117.5) * mm});
            skLineSegment(sketch, "E13.0.4.30", {"start": v(26, -118.5) * mm, "end": v(40, -118.5) * mm});
            skLineSegment(sketch, "E13.0.4.31", {"start": v(20, -104.5) * mm, "end": v(20, -117.5) * mm});
            skLineSegment(sketch, "E13.0.4.32", {"start": v(-16, -118.5) * mm, "end": v(-2, -118.5) * mm});
            skPoint(sketch, "E13.0.4.33", {"position": v(25, -103.5) * mm});
            skPoint(sketch, "E13.0.4.34", {"position": v(-17, -103.5) * mm});
            skPoint(sketch, "E13.0.4.35", {"position": v(-43, -118.5) * mm});
            skLineSegment(sketch, "E13.0.4.36", {"start": v(-37, -118.5) * mm, "end": v(-23, -118.5) * mm});
            skLineSegment(sketch, "E13.0.4.37", {"start": v(-22, -104.5) * mm, "end": v(-22, -117.5) * mm});
            skLineSegment(sketch, "E13.0.4.38", {"start": v(-37, -103.5) * mm, "end": v(-23, -103.5) * mm});
            skLineSegment(sketch, "E13.0.4.39", {"start": v(-59, -104.5) * mm, "end": v(-59, -117.5) * mm});
            skLineSegment(sketch, "E13.0.4.40", {"start": v(-43, -104.5) * mm, "end": v(-43, -117.5) * mm});
            skLineSegment(sketch, "E13.0.4.41", {"start": v(47, -103.5) * mm, "end": v(61, -103.5) * mm});
            skLineSegment(sketch, "E13.0.4.42", {"start": v(41, -104.5) * mm, "end": v(41, -117.5) * mm});
            skLineSegment(sketch, "E13.0.4.43", {"start": v(5, -103.5) * mm, "end": v(19, -103.5) * mm});
            skLineSegment(sketch, "E13.0.4.44", {"start": v(-1, -104.5) * mm, "end": v(-1, -117.5) * mm});
            skLineSegment(sketch, "E13.0.4.45", {"start": v(-38, -104.5) * mm, "end": v(-38, -117.5) * mm});
            skPoint(sketch, "E13.0.4.46", {"position": v(-43, -103.5) * mm});
            skLineSegment(sketch, "E13.0.4.47", {"start": v(-58, -103.5) * mm, "end": v(-44, -103.5) * mm});
            skLineSegment(sketch, "E13.0.4.48", {"start": v(-58, -118.5) * mm, "end": v(-44, -118.5) * mm});
            skArc(sketch, "E13.0.4.49", {"start": v(19, -118.5) * mm, "mid": v(19.7, -118.2) * mm, "end": v(20, -117.5) * mm});
            skArc(sketch, "E13.0.4.50", {"start": v(62, -104.5) * mm, "mid": v(61.7, -103.79) * mm, "end": v(61, -103.5) * mm});
            skArc(sketch, "E13.0.4.51", {"start": v(47, -103.5) * mm, "mid": v(46.3, -103.79) * mm, "end": v(46, -104.5) * mm});
            skArc(sketch, "E13.0.4.52", {"start": v(25, -117.5) * mm, "mid": v(25.3, -118.2) * mm, "end": v(26, -118.5) * mm});
            skArc(sketch, "E13.0.4.53", {"start": v(20, -104.5) * mm, "mid": v(19.7, -103.79) * mm, "end": v(19, -103.5) * mm});
            skArc(sketch, "E13.0.4.54", {"start": v(-37, -103.5) * mm, "mid": v(-37.7, -103.79) * mm, "end": v(-38, -104.5) * mm});
            skArc(sketch, "E13.0.4.55", {"start": v(-2, -118.5) * mm, "mid": v(-1.3, -118.2) * mm, "end": v(-1, -117.5) * mm});
            skArc(sketch, "E13.0.4.56", {"start": v(5, -103.5) * mm, "mid": v(4.3, -103.79) * mm, "end": v(4, -104.5) * mm});
            skArc(sketch, "E13.0.4.57", {"start": v(61, -118.5) * mm, "mid": v(61.7, -118.2) * mm, "end": v(62, -117.5) * mm});
            skArc(sketch, "E13.0.4.58", {"start": v(-17, -117.5) * mm, "mid": v(-16.7, -118.2) * mm, "end": v(-16, -118.5) * mm});
            skArc(sketch, "E13.0.4.59", {"start": v(4, -117.5) * mm, "mid": v(4.3, -118.2) * mm, "end": v(5, -118.5) * mm});
            skArc(sketch, "E13.0.4.60", {"start": v(40, -118.5) * mm, "mid": v(40.7, -118.2) * mm, "end": v(41, -117.5) * mm});
            skArc(sketch, "E13.0.4.61", {"start": v(-23, -118.5) * mm, "mid": v(-22.3, -118.2) * mm, "end": v(-22, -117.5) * mm});
            skArc(sketch, "E13.0.4.62", {"start": v(-38, -117.5) * mm, "mid": v(-37.7, -118.2) * mm, "end": v(-37, -118.5) * mm});
            skArc(sketch, "E13.0.4.63", {"start": v(-22, -104.5) * mm, "mid": v(-22.3, -103.79) * mm, "end": v(-23, -103.5) * mm});
            skArc(sketch, "E13.0.4.64", {"start": v(46, -117.5) * mm, "mid": v(46.3, -118.2) * mm, "end": v(47, -118.5) * mm});
            skArc(sketch, "E13.0.4.65", {"start": v(41, -104.5) * mm, "mid": v(40.7, -103.79) * mm, "end": v(40, -103.5) * mm});
            skArc(sketch, "E13.0.4.66", {"start": v(-1, -104.5) * mm, "mid": v(-1.3, -103.79) * mm, "end": v(-2, -103.5) * mm});
            skArc(sketch, "E13.0.4.67", {"start": v(-44, -118.5) * mm, "mid": v(-43.3, -118.2) * mm, "end": v(-43, -117.5) * mm});
            skArc(sketch, "E13.0.4.68", {"start": v(-58, -103.5) * mm, "mid": v(-58.7, -103.79) * mm, "end": v(-59, -104.5) * mm});
            skArc(sketch, "E13.0.4.69", {"start": v(26, -103.5) * mm, "mid": v(25.3, -103.79) * mm, "end": v(25, -104.5) * mm});
            skArc(sketch, "E13.0.4.70", {"start": v(-16, -103.5) * mm, "mid": v(-16.7, -103.79) * mm, "end": v(-17, -104.5) * mm});
            skArc(sketch, "E13.0.4.71", {"start": v(-43, -104.5) * mm, "mid": v(-43.3, -103.79) * mm, "end": v(-44, -103.5) * mm});
            skArc(sketch, "E13.0.4.72", {"start": v(-59, -117.5) * mm, "mid": v(-58.7, -118.2) * mm, "end": v(-58, -118.5) * mm});
            skLineSegment(sketch, "E13.direction1", {"start": v(-59, -34.5) * mm, "end": v(-34, -34.5) * mm, "construction": true});
            skLineSegment(sketch, "E13.direction2", {"start": v(-59, -34.5) * mm, "end": v(-59, -55.5) * mm, "construction": true});
            skLineSegment(sketch, "E14", {"start": v(41, -96.5) * mm, "end": v(41, -104.5) * mm});
            skLineSegment(sketch, "E15", {"start": v(25, -96.5) * mm, "end": v(25, -104.5) * mm});
            skSolve(sketch);
        }
        {
            var Q0;
            Q0=makeQuery(id+"F6.imprint","IMPRINT",FACE,{"disambiguationData":[TD([[makeQuery(id+"F6.imprint","IMPRINT",EDGE,{"derivedFrom":sQuery(id+"F6.wireOp",EDGE,"E7.bottom")}),-1.0]])]});
            extrude(context, id + "F7", {"entities" : qUnion([Q0]), "operationType" : NewBodyOperationType.REMOVE, "oppositeDirection" : true, "depth" : 2 * mm, "offsetDistance" : 25 * mm});
        }
        {
            var Q0;
            Q0=makeQuery(id+"F6.imprint","IMPRINT",FACE,{"disambiguationData":[TD([[makeQuery(id+"F6.imprint","IMPRINT",EDGE,{"derivedFrom":sQuery(id+"F6.wireOp",EDGE,"E13.0.4.18")}),1.0]])]});
            var Q1;
            Q1=makeQuery(id+"F6.imprint","IMPRINT",FACE,{"disambiguationData":[TD([[makeQuery(id+"F6.imprint","IMPRINT",EDGE,{"derivedFrom":sQuery(id+"F6.wireOp",EDGE,"E13.0.4.36")}),1.0]])]});
            var Q2;
            Q2=makeQuery(id+"F6.imprint","IMPRINT",FACE,{"disambiguationData":[TD([[makeQuery(id+"F6.imprint","IMPRINT",EDGE,{"derivedFrom":sQuery(id+"F6.wireOp",EDGE,"E13.0.4.2")}),-1.0]])]});
            var Q3;
            Q3=makeQuery(id+"F6.imprint","IMPRINT",FACE,{"disambiguationData":[TD([[makeQuery(id+"F6.imprint","IMPRINT",EDGE,{"derivedFrom":sQuery(id+"F6.wireOp",EDGE,"E13.0.4.39")}),1.0]])]});
            var Q4;
            Q4=makeQuery(id+"F6.imprint","IMPRINT",FACE,{"disambiguationData":[TD([[makeQuery(id+"F6.imprint","IMPRINT",EDGE,{"derivedFrom":sQuery(id+"F6.wireOp",EDGE,"E13.0.3.39")}),1.0]])]});
            var Q5;
            Q5=makeQuery(id+"F6.imprint","IMPRINT",FACE,{"disambiguationData":[TD([[makeQuery(id+"F6.imprint","IMPRINT",EDGE,{"derivedFrom":sQuery(id+"F6.wireOp",EDGE,"E13.0.4.4")}),1.0]])]});
            var Q6;
            Q6=makeQuery(id+"F6.imprint","IMPRINT",FACE,{"disambiguationData":[TD([[makeQuery(id+"F6.imprint","IMPRINT",EDGE,{"derivedFrom":sQuery(id+"F6.wireOp",EDGE,"E13.0.1.4")}),1.0]])]});
            var Q7;
            Q7=makeQuery(id+"F6.imprint","IMPRINT",FACE,{"disambiguationData":[TD([[makeQuery(id+"F6.imprint","IMPRINT",EDGE,{"derivedFrom":sQuery(id+"F6.wireOp",EDGE,"E13.0.3.36")}),1.0]])]});
            var Q8;
            Q8=makeQuery(id+"F6.imprint","IMPRINT",FACE,{"disambiguationData":[TD([[makeQuery(id+"F6.imprint","IMPRINT",EDGE,{"derivedFrom":sQuery(id+"F6.wireOp",EDGE,"E12.4.0.1")}),1.0]])]});
            var Q9;
            Q9=makeQuery(id+"F6.imprint","IMPRINT",FACE,{"disambiguationData":[TD([[makeQuery(id+"F6.imprint","IMPRINT",EDGE,{"derivedFrom":sQuery(id+"F6.wireOp",EDGE,"E13.0.1.36")}),1.0]])]});
            var Q10;
            Q10=makeQuery(id+"F6.imprint","IMPRINT",FACE,{"disambiguationData":[TD([[makeQuery(id+"F6.imprint","IMPRINT",EDGE,{"derivedFrom":sQuery(id+"F6.wireOp",EDGE,"E13.0.1.18")}),1.0]])]});
            var Q11;
            Q11=makeQuery(id+"F6.imprint","IMPRINT",FACE,{"disambiguationData":[TD([[makeQuery(id+"F6.imprint","IMPRINT",EDGE,{"derivedFrom":sQuery(id+"F6.wireOp",EDGE,"E13.0.1.39")}),1.0]])]});
            var Q12;
            Q12=makeQuery(id+"F6.imprint","IMPRINT",FACE,{"disambiguationData":[TD([[makeQuery(id+"F6.imprint","IMPRINT",EDGE,{"derivedFrom":sQuery(id+"F6.wireOp",EDGE,"E13.0.3.30")}),-1.0]])]});
            var Q13;
            Q13=makeQuery(id+"F6.imprint","IMPRINT",FACE,{"disambiguationData":[TD([[makeQuery(id+"F6.imprint","IMPRINT",EDGE,{"derivedFrom":sQuery(id+"F6.wireOp",EDGE,"E13.0.3.1")}),-1.0]])]});
            var Q14;
            Q14=makeQuery(id+"F6.imprint","IMPRINT",FACE,{"disambiguationData":[TD([[makeQuery(id+"F6.imprint","IMPRINT",EDGE,{"derivedFrom":sQuery(id+"F6.wireOp",EDGE,"E13.0.4.1")}),-1.0]])]});
            var Q15;
            Q15=makeQuery(id+"F6.imprint","IMPRINT",FACE,{"disambiguationData":[TD([[makeQuery(id+"F6.imprint","IMPRINT",EDGE,{"derivedFrom":sQuery(id+"F6.wireOp",EDGE,"E13.0.2.18")}),1.0]])]});
            var Q16;
            Q16=makeQuery(id+"F6.imprint","IMPRINT",FACE,{"disambiguationData":[TD([[makeQuery(id+"F6.imprint","IMPRINT",EDGE,{"derivedFrom":sQuery(id+"F6.wireOp",EDGE,"E13.0.2.36")}),1.0]])]});
            var Q17;
            Q17=makeQuery(id+"F6.imprint","IMPRINT",FACE,{"disambiguationData":[TD([[makeQuery(id+"F6.imprint","IMPRINT",EDGE,{"derivedFrom":sQuery(id+"F6.wireOp",EDGE,"E13.0.2.39")}),1.0]])]});
            var Q18;
            Q18=makeQuery(id+"F6.imprint","IMPRINT",FACE,{"disambiguationData":[TD([[makeQuery(id+"F6.imprint","IMPRINT",EDGE,{"derivedFrom":sQuery(id+"F6.wireOp",EDGE,"E12.5.0.1")}),1.0]])]});
            var Q19;
            Q19=makeQuery(id+"F6.imprint","IMPRINT",FACE,{"disambiguationData":[TD([[makeQuery(id+"F6.imprint","IMPRINT",EDGE,{"derivedFrom":sQuery(id+"F6.wireOp",EDGE,"E13.0.3.2")}),-1.0]])]});
            var Q20;
            Q20=makeQuery(id+"F6.imprint","IMPRINT",FACE,{"disambiguationData":[TD([[makeQuery(id+"F6.imprint","IMPRINT",EDGE,{"derivedFrom":sQuery(id+"F6.wireOp",EDGE,"E13.0.1.1")}),-1.0]])]});
            var Q21;
            Q21=makeQuery(id+"F6.imprint","IMPRINT",FACE,{"disambiguationData":[TD([[makeQuery(id+"F6.imprint","IMPRINT",EDGE,{"derivedFrom":sQuery(id+"F6.wireOp",EDGE,"E13.0.3.4")}),1.0]])]});
            var Q22;
            Q22=makeQuery(id+"F6.imprint","IMPRINT",FACE,{"disambiguationData":[TD([[makeQuery(id+"F6.imprint","IMPRINT",EDGE,{"derivedFrom":sQuery(id+"F6.wireOp",EDGE,"E13.0.3.18")}),1.0]])]});
            var Q23;
            Q23=makeQuery(id+"F6.imprint","IMPRINT",FACE,{"disambiguationData":[TD([[makeQuery(id+"F6.imprint","IMPRINT",EDGE,{"derivedFrom":sQuery(id+"F6.wireOp",EDGE,"E13.0.1.2")}),-1.0]])]});
            var Q24;
            Q24=makeQuery(id+"F6.imprint","IMPRINT",FACE,{"disambiguationData":[TD([[makeQuery(id+"F6.imprint","IMPRINT",EDGE,{"derivedFrom":sQuery(id+"F6.wireOp",EDGE,"E13.0.2.4")}),1.0]])]});
            var Q25;
            Q25=makeQuery(id+"F6.imprint","IMPRINT",FACE,{"disambiguationData":[TD([[makeQuery(id+"F6.imprint","IMPRINT",EDGE,{"derivedFrom":sQuery(id+"F6.wireOp",EDGE,"E13.0.2.1")}),-1.0]])]});
            var Q26;
            Q26=makeQuery(id+"F6.imprint","IMPRINT",FACE,{"disambiguationData":[TD([[makeQuery(id+"F6.imprint","IMPRINT",EDGE,{"derivedFrom":sQuery(id+"F6.wireOp",EDGE,"E13.0.2.2")}),-1.0]])]});
            var Q27;
            Q27=makeQuery(id+"F6.imprint","IMPRINT",FACE,{"disambiguationData":[TD([[makeQuery(id+"F6.imprint","IMPRINT",EDGE,{"derivedFrom":sQuery(id+"F6.wireOp",EDGE,"E6.bottom")}),-1.0]])]});
            var Q28;
            Q28=makeQuery(id+"F6.imprint","IMPRINT",FACE,{"disambiguationData":[TD([[makeQuery(id+"F6.imprint","IMPRINT",EDGE,{"derivedFrom":sQuery(id+"F6.wireOp",EDGE,"E12.1.0.1")}),1.0]])]});
            var Q29;
            Q29=makeQuery(id+"F6.imprint","IMPRINT",FACE,{"disambiguationData":[TD([[makeQuery(id+"F6.imprint","IMPRINT",EDGE,{"derivedFrom":sQuery(id+"F6.wireOp",EDGE,"E12.2.0.1")}),1.0]])]});
            var Q30;
            Q30=makeQuery(id+"F6.imprint","IMPRINT",FACE,{"disambiguationData":[TD([[makeQuery(id+"F6.imprint","IMPRINT",EDGE,{"derivedFrom":sQuery(id+"F6.wireOp",EDGE,"E12.3.0.1")}),1.0]])]});
            extrude(context, id + "F8", {"entities" : qUnion([Q0, Q1, Q2, Q3, Q4, Q5, Q6, Q7, Q8, Q9, Q10, Q11, Q12, Q13, Q14, Q15, Q16, Q17, Q18, Q19, Q20, Q21, Q22, Q23, Q24, Q25, Q26, Q27, Q28, Q29, Q30]), "operationType" : NewBodyOperationType.ADD, "depth" : 3 * mm, "offsetDistance" : 25 * mm});
        }
    });
